# Revit family: Amalphi DF
name_source: partatom
category: Plumbing Fixtures
units: mm (PartAtom-declared; Revit-internal decimal feet)

## family parameters
Always vertical = Yes
Cut with Voids When Loaded = No
Enable Cutting in Views = No
Host = Wall
Maintain Annotation Orientation = No
OmniClass Number = 23.45.00.00
OmniClass Title = Sanitary, Laundry, and Cleaning Equipment
Part Type = Normal
Room Calculation Point = No
Round Connector Dimension = Use Diameter
Shared = No

## types (3) — shared parameters
Category = Close Couple Box Sets
Ceramic = Vitreous China
Color = White
Fixing Details = Excludes Pan Fixing
Manufacturer = Lecico SA
Material = Vitreous China
Silver = Silver
Technical Dimensions = W360 x H760 x D620
URL = https://www.lecicosa.co.za
zero-valued in all types: Default Elevation

## per-type parameters (varying)
| type | Model | Product Code |
| No Seat | Amalphi DF Box Set Pan | AMPBOXDFL0NOSBE |
| With Elf Seat | Amalphi DF Box Set Pan - With Elf Seat | AMPBOXDFL0ELFBE |
| With MDF Seat | Amalphi DF Box Set Pan - With Elf Seat | AMPBOXDFL0MDFBE |

## geometry (parser evidence)
native form markers: Sweep x9
no freeform markers — native parametric forms only
